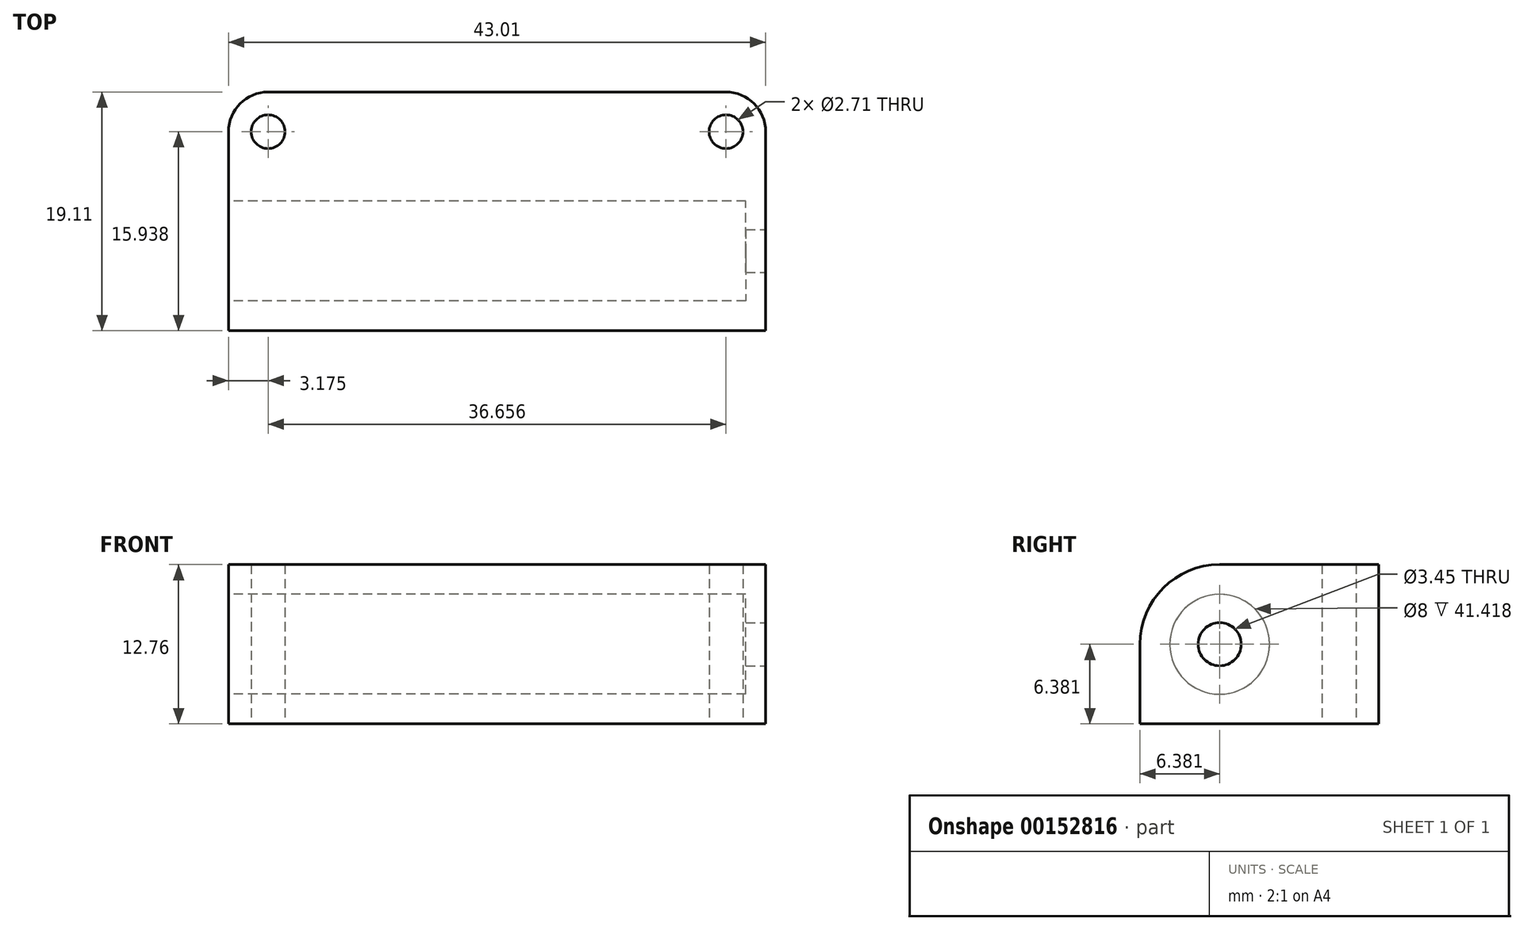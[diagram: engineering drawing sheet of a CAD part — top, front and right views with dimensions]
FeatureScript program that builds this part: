
annotation { "Feature Type Name" : "Feature", "Feature Type Description" : "" }
export const myFeature = defineFeature(function(context is Context, id is Id, definition is map)
    precondition{}
    {
        {
            var Q0;
            Q0=qCreatedBy(makeId("Top.planeOp"),FACE);
            var sketch = newSketch(context, id + "F0", { "sketchPlane" : qUnion([Q0])});
            skLineSegment(sketch, "E0.bottom", {"start": v(0, 0) * mm, "end": v(43, 0) * mm});
            skLineSegment(sketch, "E0.top", {"start": v(0, 19.11) * mm, "end": v(43, 19.11) * mm});
            skLineSegment(sketch, "E0.left", {"start": v(0, 0) * mm, "end": v(0, 19.11) * mm});
            skLineSegment(sketch, "E0.right", {"start": v(43, 0) * mm, "end": v(43, 19.11) * mm});
            skLineSegment(sketch, "E1", {"start": v(0, 15.94) * mm, "end": v(3.17, 15.94) * mm, "construction": true});
            skLineSegment(sketch, "E2", {"start": v(3.18, 15.94) * mm, "end": v(3.18, 19.11) * mm, "construction": true});
            skCircle(sketch, "E3", {"center": v(3.17, 15.94) * mm, "radius": 1.35 * mm});
            skLineSegment(sketch, "E4", {"start": v(43, 15.94) * mm, "end": v(39.83, 15.94) * mm, "construction": true});
            skCircle(sketch, "E5", {"center": v(39.83, 15.94) * mm, "radius": 1.35 * mm});
            skSolve(sketch);
        }
        {
            var Q0;
            Q0=qSketchRegion(id+"F0",true);
            extrude(context, id + "F1", {"entities" : qUnion([Q0]), "depth" : 12.76 * mm});
        }
        {
            var Q0;
            Q0=makeQuery(id+"F1.opExtrude","SWEPT_EDGE",EDGE,{"disambiguationData":[OSD([sQuery(id+"F0.wireOp",EDGE,"E0.top"),sQuery(id+"F0.wireOp",EDGE,"E0.right")])]});
            var Q1;
            Q1=makeQuery(id+"F1.opExtrude","SWEPT_EDGE",EDGE,{"disambiguationData":[OSD([sQuery(id+"F0.wireOp",EDGE,"E0.top"),sQuery(id+"F0.wireOp",EDGE,"E0.left")])]});
            fillet(context, id + "F2", {"entities" : qUnion([Q0, Q1]), "radius" : 3.17 * mm, "allowEdgeOverflow" : false});
        }
        {
            var Q0;
            Q0=makeQuery(id+"F1.opExtrude","CAP_EDGE",EDGE,{"disambiguationData":[OSD([sQuery(id+"F0.wireOp",EDGE,"E0.bottom")])],"isStart":false});
            fillet(context, id + "F3", {"entities" : qUnion([Q0]), "radius" : 6.38 * mm, "tangentPropagation" : true, "allowEdgeOverflow" : false});
        }
        {
            var Q0;
            Q0=makeQuery(id+"F1.opExtrude","SWEPT_FACE",FACE,{"disambiguationData":[OSD([sQuery(id+"F0.wireOp",EDGE,"E0.right")])]});
            var sketch = newSketch(context, id + "F4", { "sketchPlane" : qUnion([Q0])});
            skCircle(sketch, "E6", {"center": v(6.38, 6.38) * mm, "radius": 1.73 * mm});
            skSolve(sketch);
        }
        {
            var Q0;
            Q0=qSketchRegion(id+"F4",true);
            var Q1;
            Q1=makeQuery(id+"F1.opExtrude","SWEPT_FACE",FACE,{"disambiguationData":[OSD([sQuery(id+"F0.wireOp",EDGE,"E0.left")])]});
            extrude(context, id + "F5", {"entities" : qUnion([Q0]), "operationType" : NewBodyOperationType.REMOVE, "endBound" : BoundingType.UP_TO_SURFACE, "oppositeDirection" : true, "endBoundEntityFace" : qUnion([Q1]), "depth" : 25.4 * mm});
        }
        {
            var Q0;
            Q0=makeQuery(id+"F1.opExtrude","SWEPT_FACE",FACE,{"disambiguationData":[OSD([sQuery(id+"F0.wireOp",EDGE,"E0.left")])]});
            var sketch = newSketch(context, id + "F6", { "sketchPlane" : qUnion([Q0])});
            skCircle(sketch, "E7", {"center": v(-6.38, 6.38) * mm, "radius": 4 * mm});
            skSolve(sketch);
        }
        {
            var Q0;
            Q0=makeQuery(id+"F1.opExtrude","SWEPT_FACE",FACE,{"disambiguationData":[OSD([sQuery(id+"F0.wireOp",EDGE,"E0.right")])]});
            cPlane(context, id + "F7", {"entities" : qUnion([Q0]), "cplaneType" : CPlaneType.OFFSET, "offset" : 1.59 * mm, "oppositeDirection" : true, "width" : 152.4 * mm, "height" : 152.4 * mm});
        }
        {
            var Q0;
            Q0=makeQuery(id+"F6.imprint","IMPRINT",FACE,{"disambiguationData":[TD([[makeQuery(id+"F6.imprint","IMPRINT",EDGE,{"derivedFrom":sQuery(id+"F6.wireOp",EDGE,"E7")}),1.0]])]});
            var Q1;
            Q1=qCreatedBy(id+"F7.planeOp",FACE);
            extrude(context, id + "F8", {"entities" : qUnion([Q0]), "operationType" : NewBodyOperationType.REMOVE, "endBound" : BoundingType.UP_TO_SURFACE, "oppositeDirection" : true, "endBoundEntityFace" : qUnion([Q1]), "depth" : 25.4 * mm});
        }
    });
